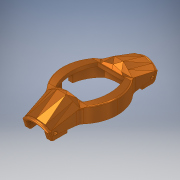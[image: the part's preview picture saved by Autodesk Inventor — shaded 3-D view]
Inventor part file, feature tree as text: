
AUTODESK INVENTOR PART (.ipt)
format: ipt  version: 2019 (Build 230136000, 136)  size: 1,625,088 bytes
history: native  units: mm
features: sketch x22, extrude x17, other x16, projected_geometry x15, plane x10, fillet x8, mirror x3, revolve x2, hole x2, sweep x1, direct_edit x1, move_body x1
ambient origin geometry x8: Origin, YZ Plane, XZ Plane, XY Plane, X Axis, Y Axis, Z Axis, Center Point
bodies: Volumenkörper1 (feature_tree), Volumenkörper2 (feature_tree), Volumenkörper3 (feature_tree), Volumenkörper5 (feature_tree), Volumenkörper8 (feature_tree), Volumenkörper6 (feature_tree), Volumenkörper7 (feature_tree)
feature tree (98):
  other  "Körper verschieben1"
  plane  "Arbeitsebene3"
  other  "Trennen1"
  plane  "Arbeitsebene1"
  sketch  "Skizze2"  dims[d2=90.0deg d3=0.8mm]
  plane  "Arbeitsebene2"
  plane  "Arbeitsebene4"
  other  "Trennen2"
  extrude  "Extrusion3"  Depth=0.8mm
  plane  "Arbeitsebene5"
  sweep  "Sweeping2"
  plane  "Arbeitsebene9"
  other  "Trennen5"
  extrude  "Extrusion4"  Depth=0.8mm TaperAngle=0.0deg
  revolve  "Umdrehung2"
  extrude  "Extrusion5"  Depth=0.45mm
  hole  "Bohrung1"  [1 undecoded]
  other  "Mittelebene"
  plane  "Arbeitsebene7"
  other  "Trennen3"
  mirror  "Spiegeln1"
  other  "Mittelebene_2"
  extrude  "Extrusion6"  Depth=3.5mm TaperAngle=0.0deg
  other  "Kombinieren2"
  fillet  "Rundung1"  Radius=2.094395mm
  fillet  "Rundung2"  Radius=6.0mm
  fillet  "Rundung3"  Radius=2.8mm
  fillet  "Rundung4"  Radius=0.5mm
  sketch  "Skizze19"  dims[d45=2.5mm d46=1.0mm]
  extrude  "Extrusion9"  Depth=0.3mm
  extrude  "Extrusion10"  Depth=1.0mm
  extrude  "Extrusion11"  TaperAngle=0.0deg  [1 undecoded]
  extrude  "Extrusion12"  Depth=12.89mm
  plane  "Arbeitsebene12"
  other  "Trennen6"
  direct_edit  "Direktbearbeitung3"
  extrude  "Extrusion13"  Depth=10.0mm TaperAngle=0.0deg
  extrude  "Extrusion14"  Depth=10.5mm
  extrude  "Extrusion15"  Depth=2.0mm TaperAngle=0.0deg
  mirror  "Spiegeln2"
  revolve  "Umdrehung3"
  plane  "Arbeitsebene14"
  other  "Trennen8"
  extrude  "Extrusion16"  TaperAngle=0.0deg  [1 undecoded]
  fillet  "Rundung6"  Radius=0.5mm
  other  "Kombinieren3"
  fillet  "Rundung7"  Radius=0.5mm
  fillet  "Rundung8"  Radius=1.0mm
  other  "Kombinieren4"
  other  "Kombinieren5"
  other  "Trennen13"
  mirror  "Spiegeln3"
  extrude  "Extrusion17"  Depth=2.0mm
  extrude  "Extrusion18"  Depth=0.872665mm
  fillet  "Rundung9"  [1 undecoded]
  hole  "Bohrung2"  [1 undecoded]
  extrude  "Extrusion19"  Depth=3.0mm
  extrude  "Extrusion20"  Depth=0.5mm TaperAngle=0.0deg
  plane  "Arbeitsebene15"
  extrude  "Extrusion21"  Depth=0.3mm
  sketch  "Skizze6"  dims[d13=-3.141593mm d14=-3.141593mm]
  projected_geometry  "Projizierte Kontur4"
  sketch  "Skizze7"  dims[d15=0.0mm d16=0.8mm d17=0.0mm]
  sketch  "Skizze8"  dims[d20=0.0mm d21=0.0mm d22=0.45mm]
  sketch  "Skizze9"  dims[d24=0.45mm d25=1.1mm]
  projected_geometry  "Projizierte Kontur6"
  sketch  "Skizze10"  dims[d26=1.1mm d27=3.5mm d28=0.0mm d29=2.094395mm d30=6.0mm d31=0.0mm]
  projected_geometry  "Projizierte Kontur7"
  projected_geometry  "Projizierte Kontur8"
  sketch  "Skizze11"  dims[d32=1.0mm d33=6.0mm d34=4.0mm d35=2.0mm d36=90.0deg d37=8.0mm d38=20.594885mm d40=2.8mm d41=0.5mm d42=0.0mm]
  projected_geometry  "Projizierte Kontur9"
  sketch  "Skizze13"  dims[d43=2.8mm d44=0.3mm]
  projected_geometry  "Projizierte Kontur13"
  projected_geometry  "Projizierte Kontur14"
  projected_geometry  "Projizierte Kontur15"
  sketch  "Skizze21"  dims[d47=0.3mm d48=0.0mm]
  sketch  "Skizze23"  dims[d59=15.56mm d60=12.89mm]
  sketch  "Skizze25"  dims[d61=10.0mm d62=0.0mm d63=10.0mm d64=0.0mm]
  projected_geometry  "Projizierte Kontur21"
  sketch  "Skizze26"  dims[d65=11.43mm d66=10.5mm]
  sketch  "Skizze27"  dims[d67=10.0mm d68=0.0mm d69=2.0mm d70=0.0mm]
  sketch  "Skizze29"  dims[d72=-0.5mm d73=0.0mm d74=0.0mm d75=-0.5mm d76=0.5mm d77=0.0mm d78=0.5mm d79=0.0mm d80=1.0mm]
  projected_geometry  "Projizierte Kontur23"
  sketch  "Skizze30"  dims[d81=2.06mm d82=2.0mm]
  projected_geometry  "Projizierte Kontur24"
  sketch  "Skizze33"  dims[d83=0.5mm d84=0.0mm d85=0.872665mm d86=0.0mm d87=0.0mm]
  sketch  "Skizze34"  dims[d89=1.0mm d90=0.3mm]
  projected_geometry  "Projizierte Kontur25"
  sketch  "Skizze35"  dims[d91=0.3mm d93=3.0mm]
  sketch  "Skizze36"  dims[d94=1.55mm d95=0.5mm d96=0.0mm]
  projected_geometry  "Projizierte Kontur26"
  sketch  "Skizze37"  dims[d97=0.953mm d98=0.0mm d99=0.3mm]
  projected_geometry  "Projizierte Kontur27"
  projected_geometry  "Projizierte Kontur28"
  sketch  "Skizze38"  dims[d100=1.4mm d101=1.4mm d102=1.0mm d103=6.0mm d104=4.0mm d105=2.0mm d106=90.0deg d107=2.5mm d108=0.0mm d109=0.953mm d110=0.0mm d111=2.0mm d112=2.0mm d113=0.953mm d114=-7.853982mm d115=4.5mm d116=1.392mm d117=0.0mm d118=0.578mm d119=0.0mm]
  other  "brep_1"
  other  "Volumenkörper1:1"
  move_body  "Verschieben1"
note: 5 required parameter values undecoded (feature->parameter linkage not recoverable at this tier; creation-order binding heuristic only, values carry confidence <= 0.55)
